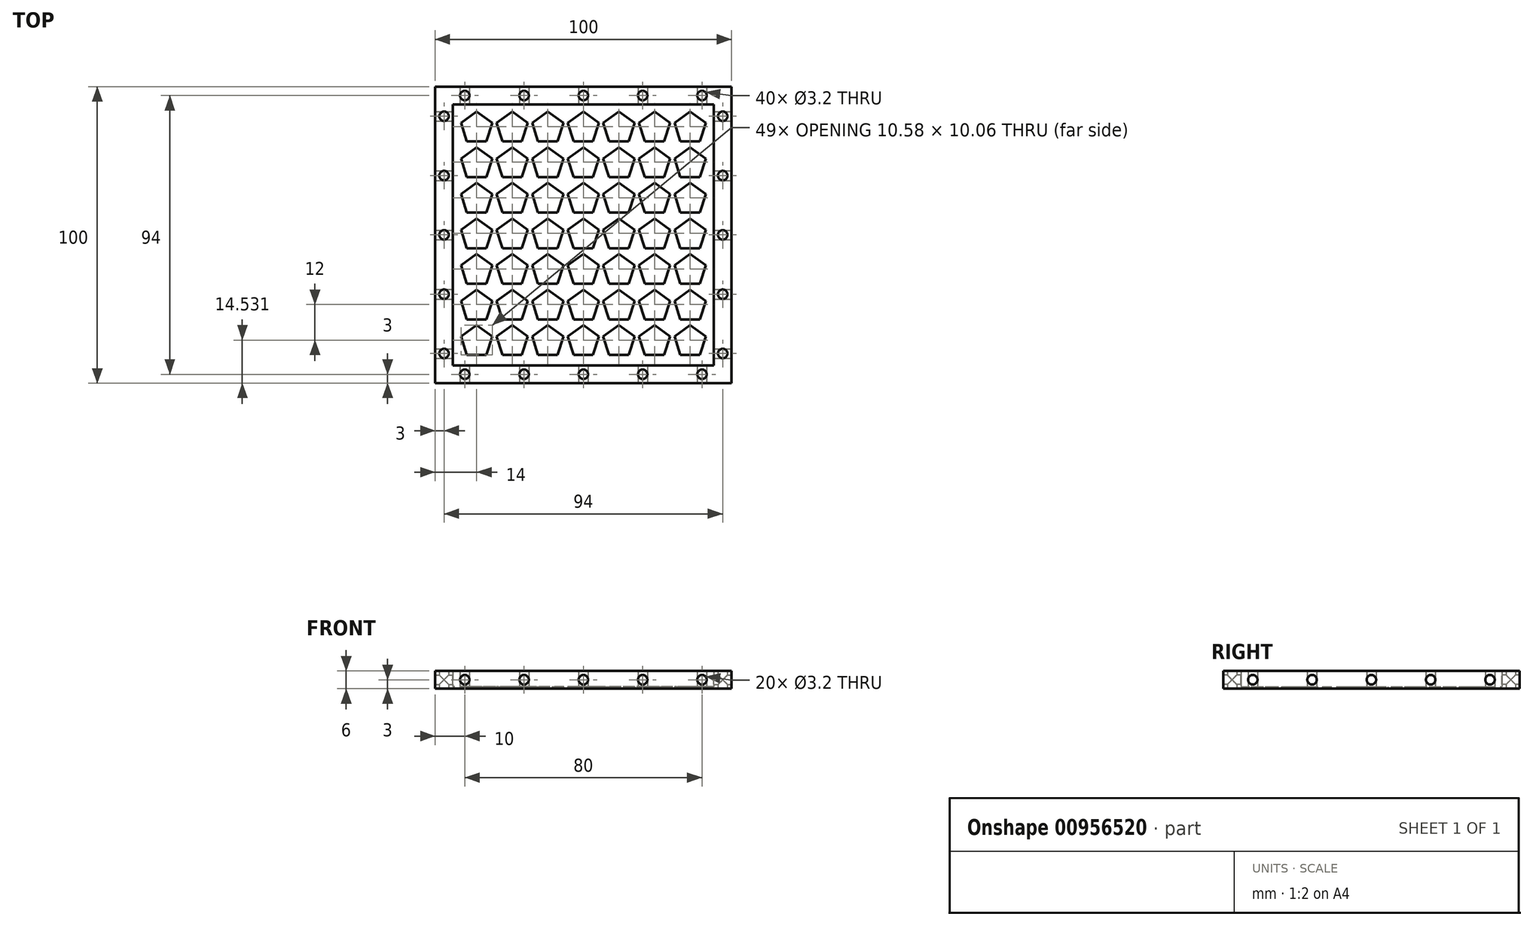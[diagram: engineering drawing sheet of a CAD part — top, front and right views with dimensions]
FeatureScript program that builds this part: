
annotation { "Feature Type Name" : "Feature", "Feature Type Description" : "" }
export const myFeature = defineFeature(function(context is Context, id is Id, definition is map)
    precondition{}
    {
        {
            var Q0;
            Q0=qCreatedBy(makeId("Top.planeOp"),FACE);
            var sketch = newSketch(context, id + "F0", { "sketchPlane" : qUnion([Q0])});
            skLineSegment(sketch, "E0.bottom", {"start": v(-50, 50) * mm, "end": v(50, 50) * mm});
            skLineSegment(sketch, "E0.top", {"start": v(-50, -50) * mm, "end": v(50, -50) * mm});
            skLineSegment(sketch, "E0.left", {"start": v(-50, 50) * mm, "end": v(-50, -50) * mm});
            skLineSegment(sketch, "E0.right", {"start": v(50, 50) * mm, "end": v(50, -50) * mm});
            skLineSegment(sketch, "E1", {"start": v(50, 50) * mm, "end": v(-50, -50) * mm, "construction": true});
            skLineSegment(sketch, "E2", {"start": v(-50, 50) * mm, "end": v(50, -50) * mm, "construction": true});
            skPoint(sketch, "E3", {"position": v(0, 0) * mm});
            skSolve(sketch);
        }
        {
            var Q0;
            Q0 = qSketchRegion(id + "F0", true);
            extrude(context, id + "F1", {"entities" : qUnion([Q0]), "depth" : .6 * mm, "offsetDistance" : 25 * mm});
        }
        {
            var Q0;
            Q0=qCreatedBy(makeId("Top.planeOp"),FACE);
            var sketch = newSketch(context, id + "F2", { "sketchPlane" : qUnion([Q0])});
            skLineSegment(sketch, "E4.bottom", {"start": v(-50, 50) * mm, "end": v(-44, 50) * mm});
            skLineSegment(sketch, "E4.top", {"start": v(-50, -50) * mm, "end": v(-44, -50) * mm});
            skLineSegment(sketch, "E4.left", {"start": v(-50, 50) * mm, "end": v(-50, -50) * mm});
            skLineSegment(sketch, "E4.right", {"start": v(-44, 50) * mm, "end": v(-44, -50) * mm});
            skLineSegment(sketch, "E5.MirrorCS", {"start": v(50, 50) * mm, "end": v(44, 50) * mm});
            skLineSegment(sketch, "E6.MirrorCS", {"start": v(50, -50) * mm, "end": v(44, -50) * mm});
            skLineSegment(sketch, "E7.MirrorCS", {"start": v(50, 50) * mm, "end": v(50, -50) * mm});
            skLineSegment(sketch, "E8.MirrorCS", {"start": v(44, 50) * mm, "end": v(44, -50) * mm});
            skLineSegment(sketch, "E9.bottom", {"start": v(-44, 50) * mm, "end": v(44, 50) * mm});
            skLineSegment(sketch, "E9.top", {"start": v(-44, 44) * mm, "end": v(44, 44) * mm});
            skLineSegment(sketch, "E9.left", {"start": v(-44, 50) * mm, "end": v(-44, 44) * mm});
            skLineSegment(sketch, "E9.right", {"start": v(44, 50) * mm, "end": v(44, 44) * mm});
            skLineSegment(sketch, "E10.MirrorCS", {"start": v(44, -50) * mm, "end": v(44, -44) * mm});
            skLineSegment(sketch, "E11.MirrorCS", {"start": v(-44, -50) * mm, "end": v(-44, -44) * mm});
            skLineSegment(sketch, "E12.MirrorCS", {"start": v(-44, -50) * mm, "end": v(44, -50) * mm});
            skLineSegment(sketch, "E13.MirrorCS", {"start": v(-44, -44) * mm, "end": v(44, -44) * mm});
            skSolve(sketch);
        }
        {
            var Q0;
            Q0 = qSketchRegion(id + "F2", true);
            extrude(context, id + "F3", {"entities" : qUnion([Q0]), "operationType" : NewBodyOperationType.ADD, "depth" : 6 * mm, "offsetDistance" : 25 * mm});
        }
        {
            var Q0;
            Q0=qCreatedBy(makeId("Top.planeOp"),FACE);
            var sketch = newSketch(context, id + "F4", { "sketchPlane" : qUnion([Q0])});
            skCircle(sketch, "E14.cCircle", {"center": v(-36, 36) * mm, "radius": 4.5 * mm, "construction": true});
            skLineSegment(sketch, "E14.0", {"start": v(-30.7, 37.72) * mm, "end": v(-32.73, 31.5) * mm});
            skLineSegment(sketch, "E14.1", {"start": v(-32.73, 31.5) * mm, "end": v(-39.27, 31.5) * mm});
            skLineSegment(sketch, "E14.2", {"start": v(-39.27, 31.5) * mm, "end": v(-41.3, 37.72) * mm});
            skLineSegment(sketch, "E14.3", {"start": v(-41.3, 37.72) * mm, "end": v(-36, 41.56) * mm});
            skLineSegment(sketch, "E14.4", {"start": v(-36, 41.56) * mm, "end": v(-30.7, 37.72) * mm});
            skPoint(sketch, "E14.0.midPoint", {"position": v(-31.72, 34.6) * mm});
            skLineSegment(sketch, "E15.0.1.0", {"start": v(-36, 29.56) * mm, "end": v(-30.7, 25.72) * mm});
            skLineSegment(sketch, "E15.0.1.1", {"start": v(-41.3, 25.72) * mm, "end": v(-36, 29.56) * mm});
            skPoint(sketch, "E15.0.1.2", {"position": v(-31.72, 22.6) * mm});
            skCircle(sketch, "E15.0.1.3", {"center": v(-36, 24) * mm, "radius": 4.5 * mm, "construction": true});
            skLineSegment(sketch, "E15.0.1.4", {"start": v(-30.7, 25.72) * mm, "end": v(-32.73, 19.5) * mm});
            skLineSegment(sketch, "E15.0.1.5", {"start": v(-32.73, 19.5) * mm, "end": v(-39.27, 19.5) * mm});
            skLineSegment(sketch, "E15.0.1.6", {"start": v(-39.27, 19.5) * mm, "end": v(-41.3, 25.72) * mm});
            skLineSegment(sketch, "E15.0.2.0", {"start": v(-36, 17.56) * mm, "end": v(-30.7, 13.72) * mm});
            skLineSegment(sketch, "E15.0.2.1", {"start": v(-41.3, 13.72) * mm, "end": v(-36, 17.56) * mm});
            skPoint(sketch, "E15.0.2.2", {"position": v(-31.72, 10.6) * mm});
            skCircle(sketch, "E15.0.2.3", {"center": v(-36, 12) * mm, "radius": 4.5 * mm, "construction": true});
            skLineSegment(sketch, "E15.0.2.4", {"start": v(-30.7, 13.72) * mm, "end": v(-32.73, 7.5) * mm});
            skLineSegment(sketch, "E15.0.2.5", {"start": v(-32.73, 7.5) * mm, "end": v(-39.27, 7.5) * mm});
            skLineSegment(sketch, "E15.0.2.6", {"start": v(-39.27, 7.5) * mm, "end": v(-41.3, 13.72) * mm});
            skLineSegment(sketch, "E15.0.3.0", {"start": v(-36, 5.56) * mm, "end": v(-30.7, 1.72) * mm});
            skLineSegment(sketch, "E15.0.3.1", {"start": v(-41.3, 1.72) * mm, "end": v(-36, 5.56) * mm});
            skPoint(sketch, "E15.0.3.2", {"position": v(-31.72, -1.4) * mm});
            skCircle(sketch, "E15.0.3.3", {"center": v(-36, 0) * mm, "radius": 4.5 * mm, "construction": true});
            skLineSegment(sketch, "E15.0.3.4", {"start": v(-30.7, 1.72) * mm, "end": v(-32.73, -4.5) * mm});
            skLineSegment(sketch, "E15.0.3.5", {"start": v(-32.73, -4.5) * mm, "end": v(-39.27, -4.5) * mm});
            skLineSegment(sketch, "E15.0.3.6", {"start": v(-39.27, -4.5) * mm, "end": v(-41.3, 1.72) * mm});
            skLineSegment(sketch, "E15.0.4.0", {"start": v(-36, -6.44) * mm, "end": v(-30.7, -10.28) * mm});
            skLineSegment(sketch, "E15.0.4.1", {"start": v(-41.3, -10.28) * mm, "end": v(-36, -6.44) * mm});
            skPoint(sketch, "E15.0.4.2", {"position": v(-31.72, -13.4) * mm});
            skCircle(sketch, "E15.0.4.3", {"center": v(-36, -12) * mm, "radius": 4.5 * mm, "construction": true});
            skLineSegment(sketch, "E15.0.4.4", {"start": v(-30.7, -10.28) * mm, "end": v(-32.73, -16.5) * mm});
            skLineSegment(sketch, "E15.0.4.5", {"start": v(-32.73, -16.5) * mm, "end": v(-39.27, -16.5) * mm});
            skLineSegment(sketch, "E15.0.4.6", {"start": v(-39.27, -16.5) * mm, "end": v(-41.3, -10.28) * mm});
            skLineSegment(sketch, "E15.0.5.0", {"start": v(-36, -18.44) * mm, "end": v(-30.7, -22.28) * mm});
            skLineSegment(sketch, "E15.0.5.1", {"start": v(-41.3, -22.28) * mm, "end": v(-36, -18.44) * mm});
            skPoint(sketch, "E15.0.5.2", {"position": v(-31.72, -25.4) * mm});
            skCircle(sketch, "E15.0.5.3", {"center": v(-36, -24) * mm, "radius": 4.5 * mm, "construction": true});
            skLineSegment(sketch, "E15.0.5.4", {"start": v(-30.7, -22.28) * mm, "end": v(-32.73, -28.5) * mm});
            skLineSegment(sketch, "E15.0.5.5", {"start": v(-32.73, -28.5) * mm, "end": v(-39.27, -28.5) * mm});
            skLineSegment(sketch, "E15.0.5.6", {"start": v(-39.27, -28.5) * mm, "end": v(-41.3, -22.28) * mm});
            skLineSegment(sketch, "E15.1.0.0", {"start": v(-24, 41.56) * mm, "end": v(-18.7, 37.72) * mm});
            skLineSegment(sketch, "E15.1.0.1", {"start": v(-29.3, 37.72) * mm, "end": v(-24, 41.56) * mm});
            skPoint(sketch, "E15.1.0.2", {"position": v(-19.72, 34.6) * mm});
            skCircle(sketch, "E15.1.0.3", {"center": v(-24, 36) * mm, "radius": 4.5 * mm, "construction": true});
            skLineSegment(sketch, "E15.1.0.4", {"start": v(-18.7, 37.72) * mm, "end": v(-20.73, 31.5) * mm});
            skLineSegment(sketch, "E15.1.0.5", {"start": v(-20.73, 31.5) * mm, "end": v(-27.27, 31.5) * mm});
            skLineSegment(sketch, "E15.1.0.6", {"start": v(-27.27, 31.5) * mm, "end": v(-29.3, 37.72) * mm});
            skLineSegment(sketch, "E15.1.1.0", {"start": v(-24, 29.56) * mm, "end": v(-18.7, 25.72) * mm});
            skLineSegment(sketch, "E15.1.1.1", {"start": v(-29.3, 25.72) * mm, "end": v(-24, 29.56) * mm});
            skPoint(sketch, "E15.1.1.2", {"position": v(-19.72, 22.6) * mm});
            skCircle(sketch, "E15.1.1.3", {"center": v(-24, 24) * mm, "radius": 4.5 * mm, "construction": true});
            skLineSegment(sketch, "E15.1.1.4", {"start": v(-18.7, 25.72) * mm, "end": v(-20.73, 19.5) * mm});
            skLineSegment(sketch, "E15.1.1.5", {"start": v(-20.73, 19.5) * mm, "end": v(-27.27, 19.5) * mm});
            skLineSegment(sketch, "E15.1.1.6", {"start": v(-27.27, 19.5) * mm, "end": v(-29.3, 25.72) * mm});
            skLineSegment(sketch, "E15.1.2.0", {"start": v(-24, 17.56) * mm, "end": v(-18.7, 13.72) * mm});
            skLineSegment(sketch, "E15.1.2.1", {"start": v(-29.3, 13.72) * mm, "end": v(-24, 17.56) * mm});
            skPoint(sketch, "E15.1.2.2", {"position": v(-19.72, 10.6) * mm});
            skCircle(sketch, "E15.1.2.3", {"center": v(-24, 12) * mm, "radius": 4.5 * mm, "construction": true});
            skLineSegment(sketch, "E15.1.2.4", {"start": v(-18.7, 13.72) * mm, "end": v(-20.73, 7.5) * mm});
            skLineSegment(sketch, "E15.1.2.5", {"start": v(-20.73, 7.5) * mm, "end": v(-27.27, 7.5) * mm});
            skLineSegment(sketch, "E15.1.2.6", {"start": v(-27.27, 7.5) * mm, "end": v(-29.3, 13.72) * mm});
            skLineSegment(sketch, "E15.1.3.0", {"start": v(-24, 5.56) * mm, "end": v(-18.7, 1.72) * mm});
            skLineSegment(sketch, "E15.1.3.1", {"start": v(-29.3, 1.72) * mm, "end": v(-24, 5.56) * mm});
            skPoint(sketch, "E15.1.3.2", {"position": v(-19.72, -1.4) * mm});
            skCircle(sketch, "E15.1.3.3", {"center": v(-24, 0) * mm, "radius": 4.5 * mm, "construction": true});
            skLineSegment(sketch, "E15.1.3.4", {"start": v(-18.7, 1.72) * mm, "end": v(-20.73, -4.5) * mm});
            skLineSegment(sketch, "E15.1.3.5", {"start": v(-20.73, -4.5) * mm, "end": v(-27.27, -4.5) * mm});
            skLineSegment(sketch, "E15.1.3.6", {"start": v(-27.27, -4.5) * mm, "end": v(-29.3, 1.72) * mm});
            skLineSegment(sketch, "E15.1.4.0", {"start": v(-24, -6.44) * mm, "end": v(-18.7, -10.28) * mm});
            skLineSegment(sketch, "E15.1.4.1", {"start": v(-29.3, -10.28) * mm, "end": v(-24, -6.44) * mm});
            skPoint(sketch, "E15.1.4.2", {"position": v(-19.72, -13.4) * mm});
            skCircle(sketch, "E15.1.4.3", {"center": v(-24, -12) * mm, "radius": 4.5 * mm, "construction": true});
            skLineSegment(sketch, "E15.1.4.4", {"start": v(-18.7, -10.28) * mm, "end": v(-20.73, -16.5) * mm});
            skLineSegment(sketch, "E15.1.4.5", {"start": v(-20.73, -16.5) * mm, "end": v(-27.27, -16.5) * mm});
            skLineSegment(sketch, "E15.1.4.6", {"start": v(-27.27, -16.5) * mm, "end": v(-29.3, -10.28) * mm});
            skLineSegment(sketch, "E15.1.5.0", {"start": v(-24, -18.44) * mm, "end": v(-18.7, -22.28) * mm});
            skLineSegment(sketch, "E15.1.5.1", {"start": v(-29.3, -22.28) * mm, "end": v(-24, -18.44) * mm});
            skPoint(sketch, "E15.1.5.2", {"position": v(-19.72, -25.4) * mm});
            skCircle(sketch, "E15.1.5.3", {"center": v(-24, -24) * mm, "radius": 4.5 * mm, "construction": true});
            skLineSegment(sketch, "E15.1.5.4", {"start": v(-18.7, -22.28) * mm, "end": v(-20.73, -28.5) * mm});
            skLineSegment(sketch, "E15.1.5.5", {"start": v(-20.73, -28.5) * mm, "end": v(-27.27, -28.5) * mm});
            skLineSegment(sketch, "E15.1.5.6", {"start": v(-27.27, -28.5) * mm, "end": v(-29.3, -22.28) * mm});
            skLineSegment(sketch, "E15.2.0.0", {"start": v(-12, 41.56) * mm, "end": v(-6.7, 37.72) * mm});
            skLineSegment(sketch, "E15.2.0.1", {"start": v(-17.3, 37.72) * mm, "end": v(-12, 41.56) * mm});
            skPoint(sketch, "E15.2.0.2", {"position": v(-7.72, 34.6) * mm});
            skCircle(sketch, "E15.2.0.3", {"center": v(-12, 36) * mm, "radius": 4.5 * mm, "construction": true});
            skLineSegment(sketch, "E15.2.0.4", {"start": v(-6.7, 37.72) * mm, "end": v(-8.73, 31.5) * mm});
            skLineSegment(sketch, "E15.2.0.5", {"start": v(-8.73, 31.5) * mm, "end": v(-15.27, 31.5) * mm});
            skLineSegment(sketch, "E15.2.0.6", {"start": v(-15.27, 31.5) * mm, "end": v(-17.3, 37.72) * mm});
            skLineSegment(sketch, "E15.2.1.0", {"start": v(-12, 29.56) * mm, "end": v(-6.7, 25.72) * mm});
            skLineSegment(sketch, "E15.2.1.1", {"start": v(-17.3, 25.72) * mm, "end": v(-12, 29.56) * mm});
            skPoint(sketch, "E15.2.1.2", {"position": v(-7.72, 22.6) * mm});
            skCircle(sketch, "E15.2.1.3", {"center": v(-12, 24) * mm, "radius": 4.5 * mm, "construction": true});
            skLineSegment(sketch, "E15.2.1.4", {"start": v(-6.7, 25.72) * mm, "end": v(-8.73, 19.5) * mm});
            skLineSegment(sketch, "E15.2.1.5", {"start": v(-8.73, 19.5) * mm, "end": v(-15.27, 19.5) * mm});
            skLineSegment(sketch, "E15.2.1.6", {"start": v(-15.27, 19.5) * mm, "end": v(-17.3, 25.72) * mm});
            skLineSegment(sketch, "E15.2.2.0", {"start": v(-12, 17.56) * mm, "end": v(-6.7, 13.72) * mm});
            skLineSegment(sketch, "E15.2.2.1", {"start": v(-17.3, 13.72) * mm, "end": v(-12, 17.56) * mm});
            skPoint(sketch, "E15.2.2.2", {"position": v(-7.72, 10.6) * mm});
            skCircle(sketch, "E15.2.2.3", {"center": v(-12, 12) * mm, "radius": 4.5 * mm, "construction": true});
            skLineSegment(sketch, "E15.2.2.4", {"start": v(-6.7, 13.72) * mm, "end": v(-8.73, 7.5) * mm});
            skLineSegment(sketch, "E15.2.2.5", {"start": v(-8.73, 7.5) * mm, "end": v(-15.27, 7.5) * mm});
            skLineSegment(sketch, "E15.2.2.6", {"start": v(-15.27, 7.5) * mm, "end": v(-17.3, 13.72) * mm});
            skLineSegment(sketch, "E15.2.3.0", {"start": v(-12, 5.56) * mm, "end": v(-6.7, 1.72) * mm});
            skLineSegment(sketch, "E15.2.3.1", {"start": v(-17.3, 1.72) * mm, "end": v(-12, 5.56) * mm});
            skPoint(sketch, "E15.2.3.2", {"position": v(-7.72, -1.4) * mm});
            skCircle(sketch, "E15.2.3.3", {"center": v(-12, 0) * mm, "radius": 4.5 * mm, "construction": true});
            skLineSegment(sketch, "E15.2.3.4", {"start": v(-6.7, 1.72) * mm, "end": v(-8.73, -4.5) * mm});
            skLineSegment(sketch, "E15.2.3.5", {"start": v(-8.73, -4.5) * mm, "end": v(-15.27, -4.5) * mm});
            skLineSegment(sketch, "E15.2.3.6", {"start": v(-15.27, -4.5) * mm, "end": v(-17.3, 1.72) * mm});
            skLineSegment(sketch, "E15.2.4.0", {"start": v(-12, -6.44) * mm, "end": v(-6.7, -10.28) * mm});
            skLineSegment(sketch, "E15.2.4.1", {"start": v(-17.3, -10.28) * mm, "end": v(-12, -6.44) * mm});
            skPoint(sketch, "E15.2.4.2", {"position": v(-7.72, -13.4) * mm});
            skCircle(sketch, "E15.2.4.3", {"center": v(-12, -12) * mm, "radius": 4.5 * mm, "construction": true});
            skLineSegment(sketch, "E15.2.4.4", {"start": v(-6.7, -10.28) * mm, "end": v(-8.73, -16.5) * mm});
            skLineSegment(sketch, "E15.2.4.5", {"start": v(-8.73, -16.5) * mm, "end": v(-15.27, -16.5) * mm});
            skLineSegment(sketch, "E15.2.4.6", {"start": v(-15.27, -16.5) * mm, "end": v(-17.3, -10.28) * mm});
            skLineSegment(sketch, "E15.2.5.0", {"start": v(-12, -18.44) * mm, "end": v(-6.7, -22.28) * mm});
            skLineSegment(sketch, "E15.2.5.1", {"start": v(-17.3, -22.28) * mm, "end": v(-12, -18.44) * mm});
            skPoint(sketch, "E15.2.5.2", {"position": v(-7.72, -25.4) * mm});
            skCircle(sketch, "E15.2.5.3", {"center": v(-12, -24) * mm, "radius": 4.5 * mm, "construction": true});
            skLineSegment(sketch, "E15.2.5.4", {"start": v(-6.7, -22.28) * mm, "end": v(-8.73, -28.5) * mm});
            skLineSegment(sketch, "E15.2.5.5", {"start": v(-8.73, -28.5) * mm, "end": v(-15.27, -28.5) * mm});
            skLineSegment(sketch, "E15.2.5.6", {"start": v(-15.27, -28.5) * mm, "end": v(-17.3, -22.28) * mm});
            skLineSegment(sketch, "E15.3.0.0", {"start": v(0, 41.56) * mm, "end": v(5.3, 37.72) * mm});
            skLineSegment(sketch, "E15.3.0.1", {"start": v(-5.3, 37.72) * mm, "end": v(0, 41.56) * mm});
            skPoint(sketch, "E15.3.0.2", {"position": v(4.28, 34.6) * mm});
            skCircle(sketch, "E15.3.0.3", {"center": v(0, 36) * mm, "radius": 4.5 * mm, "construction": true});
            skLineSegment(sketch, "E15.3.0.4", {"start": v(5.3, 37.72) * mm, "end": v(3.27, 31.5) * mm});
            skLineSegment(sketch, "E15.3.0.5", {"start": v(3.27, 31.5) * mm, "end": v(-3.27, 31.5) * mm});
            skLineSegment(sketch, "E15.3.0.6", {"start": v(-3.27, 31.5) * mm, "end": v(-5.3, 37.72) * mm});
            skLineSegment(sketch, "E15.3.1.0", {"start": v(0, 29.56) * mm, "end": v(5.3, 25.72) * mm});
            skLineSegment(sketch, "E15.3.1.1", {"start": v(-5.3, 25.72) * mm, "end": v(0, 29.56) * mm});
            skPoint(sketch, "E15.3.1.2", {"position": v(4.28, 22.6) * mm});
            skCircle(sketch, "E15.3.1.3", {"center": v(0, 24) * mm, "radius": 4.5 * mm, "construction": true});
            skLineSegment(sketch, "E15.3.1.4", {"start": v(5.3, 25.72) * mm, "end": v(3.27, 19.5) * mm});
            skLineSegment(sketch, "E15.3.1.5", {"start": v(3.27, 19.5) * mm, "end": v(-3.27, 19.5) * mm});
            skLineSegment(sketch, "E15.3.1.6", {"start": v(-3.27, 19.5) * mm, "end": v(-5.3, 25.72) * mm});
            skLineSegment(sketch, "E15.3.2.0", {"start": v(0, 17.56) * mm, "end": v(5.3, 13.72) * mm});
            skLineSegment(sketch, "E15.3.2.1", {"start": v(-5.3, 13.72) * mm, "end": v(0, 17.56) * mm});
            skPoint(sketch, "E15.3.2.2", {"position": v(4.28, 10.6) * mm});
            skCircle(sketch, "E15.3.2.3", {"center": v(0, 12) * mm, "radius": 4.5 * mm, "construction": true});
            skLineSegment(sketch, "E15.3.2.4", {"start": v(5.3, 13.72) * mm, "end": v(3.27, 7.5) * mm});
            skLineSegment(sketch, "E15.3.2.5", {"start": v(3.27, 7.5) * mm, "end": v(-3.27, 7.5) * mm});
            skLineSegment(sketch, "E15.3.2.6", {"start": v(-3.27, 7.5) * mm, "end": v(-5.3, 13.72) * mm});
            skLineSegment(sketch, "E15.3.3.0", {"start": v(0, 5.56) * mm, "end": v(5.3, 1.72) * mm});
            skLineSegment(sketch, "E15.3.3.1", {"start": v(-5.3, 1.72) * mm, "end": v(0, 5.56) * mm});
            skPoint(sketch, "E15.3.3.2", {"position": v(4.28, -1.4) * mm});
            skCircle(sketch, "E15.3.3.3", {"center": v(0, 0) * mm, "radius": 4.5 * mm, "construction": true});
            skLineSegment(sketch, "E15.3.3.4", {"start": v(5.3, 1.72) * mm, "end": v(3.27, -4.5) * mm});
            skLineSegment(sketch, "E15.3.3.5", {"start": v(3.27, -4.5) * mm, "end": v(-3.27, -4.5) * mm});
            skLineSegment(sketch, "E15.3.3.6", {"start": v(-3.27, -4.5) * mm, "end": v(-5.3, 1.72) * mm});
            skLineSegment(sketch, "E15.3.4.0", {"start": v(0, -6.44) * mm, "end": v(5.3, -10.28) * mm});
            skLineSegment(sketch, "E15.3.4.1", {"start": v(-5.3, -10.28) * mm, "end": v(0, -6.44) * mm});
            skPoint(sketch, "E15.3.4.2", {"position": v(4.28, -13.4) * mm});
            skCircle(sketch, "E15.3.4.3", {"center": v(0, -12) * mm, "radius": 4.5 * mm, "construction": true});
            skLineSegment(sketch, "E15.3.4.4", {"start": v(5.3, -10.28) * mm, "end": v(3.27, -16.5) * mm});
            skLineSegment(sketch, "E15.3.4.5", {"start": v(3.27, -16.5) * mm, "end": v(-3.27, -16.5) * mm});
            skLineSegment(sketch, "E15.3.4.6", {"start": v(-3.27, -16.5) * mm, "end": v(-5.3, -10.28) * mm});
            skLineSegment(sketch, "E15.3.5.0", {"start": v(0, -18.44) * mm, "end": v(5.3, -22.28) * mm});
            skLineSegment(sketch, "E15.3.5.1", {"start": v(-5.3, -22.28) * mm, "end": v(0, -18.44) * mm});
            skPoint(sketch, "E15.3.5.2", {"position": v(4.28, -25.4) * mm});
            skCircle(sketch, "E15.3.5.3", {"center": v(0, -24) * mm, "radius": 4.5 * mm, "construction": true});
            skLineSegment(sketch, "E15.3.5.4", {"start": v(5.3, -22.28) * mm, "end": v(3.27, -28.5) * mm});
            skLineSegment(sketch, "E15.3.5.5", {"start": v(3.27, -28.5) * mm, "end": v(-3.27, -28.5) * mm});
            skLineSegment(sketch, "E15.3.5.6", {"start": v(-3.27, -28.5) * mm, "end": v(-5.3, -22.28) * mm});
            skLineSegment(sketch, "E15.4.0.0", {"start": v(12, 41.56) * mm, "end": v(17.3, 37.72) * mm});
            skLineSegment(sketch, "E15.4.0.1", {"start": v(6.7, 37.72) * mm, "end": v(12, 41.56) * mm});
            skPoint(sketch, "E15.4.0.2", {"position": v(16.28, 34.6) * mm});
            skCircle(sketch, "E15.4.0.3", {"center": v(12, 36) * mm, "radius": 4.5 * mm, "construction": true});
            skLineSegment(sketch, "E15.4.0.4", {"start": v(17.3, 37.72) * mm, "end": v(15.27, 31.5) * mm});
            skLineSegment(sketch, "E15.4.0.5", {"start": v(15.27, 31.5) * mm, "end": v(8.73, 31.5) * mm});
            skLineSegment(sketch, "E15.4.0.6", {"start": v(8.73, 31.5) * mm, "end": v(6.7, 37.72) * mm});
            skLineSegment(sketch, "E15.4.1.0", {"start": v(12, 29.56) * mm, "end": v(17.3, 25.72) * mm});
            skLineSegment(sketch, "E15.4.1.1", {"start": v(6.7, 25.72) * mm, "end": v(12, 29.56) * mm});
            skPoint(sketch, "E15.4.1.2", {"position": v(16.28, 22.6) * mm});
            skCircle(sketch, "E15.4.1.3", {"center": v(12, 24) * mm, "radius": 4.5 * mm, "construction": true});
            skLineSegment(sketch, "E15.4.1.4", {"start": v(17.3, 25.72) * mm, "end": v(15.27, 19.5) * mm});
            skLineSegment(sketch, "E15.4.1.5", {"start": v(15.27, 19.5) * mm, "end": v(8.73, 19.5) * mm});
            skLineSegment(sketch, "E15.4.1.6", {"start": v(8.73, 19.5) * mm, "end": v(6.7, 25.72) * mm});
            skLineSegment(sketch, "E15.4.2.0", {"start": v(12, 17.56) * mm, "end": v(17.3, 13.72) * mm});
            skLineSegment(sketch, "E15.4.2.1", {"start": v(6.7, 13.72) * mm, "end": v(12, 17.56) * mm});
            skPoint(sketch, "E15.4.2.2", {"position": v(16.28, 10.6) * mm});
            skCircle(sketch, "E15.4.2.3", {"center": v(12, 12) * mm, "radius": 4.5 * mm, "construction": true});
            skLineSegment(sketch, "E15.4.2.4", {"start": v(17.3, 13.72) * mm, "end": v(15.27, 7.5) * mm});
            skLineSegment(sketch, "E15.4.2.5", {"start": v(15.27, 7.5) * mm, "end": v(8.73, 7.5) * mm});
            skLineSegment(sketch, "E15.4.2.6", {"start": v(8.73, 7.5) * mm, "end": v(6.7, 13.72) * mm});
            skLineSegment(sketch, "E15.4.3.0", {"start": v(12, 5.56) * mm, "end": v(17.3, 1.72) * mm});
            skLineSegment(sketch, "E15.4.3.1", {"start": v(6.7, 1.72) * mm, "end": v(12, 5.56) * mm});
            skPoint(sketch, "E15.4.3.2", {"position": v(16.28, -1.4) * mm});
            skCircle(sketch, "E15.4.3.3", {"center": v(12, 0) * mm, "radius": 4.5 * mm, "construction": true});
            skLineSegment(sketch, "E15.4.3.4", {"start": v(17.3, 1.72) * mm, "end": v(15.27, -4.5) * mm});
            skLineSegment(sketch, "E15.4.3.5", {"start": v(15.27, -4.5) * mm, "end": v(8.73, -4.5) * mm});
            skLineSegment(sketch, "E15.4.3.6", {"start": v(8.73, -4.5) * mm, "end": v(6.7, 1.72) * mm});
            skLineSegment(sketch, "E15.4.4.0", {"start": v(12, -6.44) * mm, "end": v(17.3, -10.28) * mm});
            skLineSegment(sketch, "E15.4.4.1", {"start": v(6.7, -10.28) * mm, "end": v(12, -6.44) * mm});
            skPoint(sketch, "E15.4.4.2", {"position": v(16.28, -13.4) * mm});
            skCircle(sketch, "E15.4.4.3", {"center": v(12, -12) * mm, "radius": 4.5 * mm, "construction": true});
            skLineSegment(sketch, "E15.4.4.4", {"start": v(17.3, -10.28) * mm, "end": v(15.27, -16.5) * mm});
            skLineSegment(sketch, "E15.4.4.5", {"start": v(15.27, -16.5) * mm, "end": v(8.73, -16.5) * mm});
            skLineSegment(sketch, "E15.4.4.6", {"start": v(8.73, -16.5) * mm, "end": v(6.7, -10.28) * mm});
            skLineSegment(sketch, "E15.4.5.0", {"start": v(12, -18.44) * mm, "end": v(17.3, -22.28) * mm});
            skLineSegment(sketch, "E15.4.5.1", {"start": v(6.7, -22.28) * mm, "end": v(12, -18.44) * mm});
            skPoint(sketch, "E15.4.5.2", {"position": v(16.28, -25.4) * mm});
            skCircle(sketch, "E15.4.5.3", {"center": v(12, -24) * mm, "radius": 4.5 * mm, "construction": true});
            skLineSegment(sketch, "E15.4.5.4", {"start": v(17.3, -22.28) * mm, "end": v(15.27, -28.5) * mm});
            skLineSegment(sketch, "E15.4.5.5", {"start": v(15.27, -28.5) * mm, "end": v(8.73, -28.5) * mm});
            skLineSegment(sketch, "E15.4.5.6", {"start": v(8.73, -28.5) * mm, "end": v(6.7, -22.28) * mm});
            skLineSegment(sketch, "E15.5.0.0", {"start": v(24, 41.56) * mm, "end": v(29.3, 37.72) * mm});
            skLineSegment(sketch, "E15.5.0.1", {"start": v(18.7, 37.72) * mm, "end": v(24, 41.56) * mm});
            skPoint(sketch, "E15.5.0.2", {"position": v(28.28, 34.6) * mm});
            skCircle(sketch, "E15.5.0.3", {"center": v(24, 36) * mm, "radius": 4.5 * mm, "construction": true});
            skLineSegment(sketch, "E15.5.0.4", {"start": v(29.3, 37.72) * mm, "end": v(27.27, 31.5) * mm});
            skLineSegment(sketch, "E15.5.0.5", {"start": v(27.27, 31.5) * mm, "end": v(20.73, 31.5) * mm});
            skLineSegment(sketch, "E15.5.0.6", {"start": v(20.73, 31.5) * mm, "end": v(18.7, 37.72) * mm});
            skLineSegment(sketch, "E15.5.1.0", {"start": v(24, 29.56) * mm, "end": v(29.3, 25.72) * mm});
            skLineSegment(sketch, "E15.5.1.1", {"start": v(18.7, 25.72) * mm, "end": v(24, 29.56) * mm});
            skPoint(sketch, "E15.5.1.2", {"position": v(28.28, 22.6) * mm});
            skCircle(sketch, "E15.5.1.3", {"center": v(24, 24) * mm, "radius": 4.5 * mm, "construction": true});
            skLineSegment(sketch, "E15.5.1.4", {"start": v(29.3, 25.72) * mm, "end": v(27.27, 19.5) * mm});
            skLineSegment(sketch, "E15.5.1.5", {"start": v(27.27, 19.5) * mm, "end": v(20.73, 19.5) * mm});
            skLineSegment(sketch, "E15.5.1.6", {"start": v(20.73, 19.5) * mm, "end": v(18.7, 25.72) * mm});
            skLineSegment(sketch, "E15.5.2.0", {"start": v(24, 17.56) * mm, "end": v(29.3, 13.72) * mm});
            skLineSegment(sketch, "E15.5.2.1", {"start": v(18.7, 13.72) * mm, "end": v(24, 17.56) * mm});
            skPoint(sketch, "E15.5.2.2", {"position": v(28.28, 10.6) * mm});
            skCircle(sketch, "E15.5.2.3", {"center": v(24, 12) * mm, "radius": 4.5 * mm, "construction": true});
            skLineSegment(sketch, "E15.5.2.4", {"start": v(29.3, 13.72) * mm, "end": v(27.27, 7.5) * mm});
            skLineSegment(sketch, "E15.5.2.5", {"start": v(27.27, 7.5) * mm, "end": v(20.73, 7.5) * mm});
            skLineSegment(sketch, "E15.5.2.6", {"start": v(20.73, 7.5) * mm, "end": v(18.7, 13.72) * mm});
            skLineSegment(sketch, "E15.5.3.0", {"start": v(24, 5.56) * mm, "end": v(29.3, 1.72) * mm});
            skLineSegment(sketch, "E15.5.3.1", {"start": v(18.7, 1.72) * mm, "end": v(24, 5.56) * mm});
            skPoint(sketch, "E15.5.3.2", {"position": v(28.28, -1.4) * mm});
            skCircle(sketch, "E15.5.3.3", {"center": v(24, 0) * mm, "radius": 4.5 * mm, "construction": true});
            skLineSegment(sketch, "E15.5.3.4", {"start": v(29.3, 1.72) * mm, "end": v(27.27, -4.5) * mm});
            skLineSegment(sketch, "E15.5.3.5", {"start": v(27.27, -4.5) * mm, "end": v(20.73, -4.5) * mm});
            skLineSegment(sketch, "E15.5.3.6", {"start": v(20.73, -4.5) * mm, "end": v(18.7, 1.72) * mm});
            skLineSegment(sketch, "E15.5.4.0", {"start": v(24, -6.44) * mm, "end": v(29.3, -10.28) * mm});
            skLineSegment(sketch, "E15.5.4.1", {"start": v(18.7, -10.28) * mm, "end": v(24, -6.44) * mm});
            skPoint(sketch, "E15.5.4.2", {"position": v(28.28, -13.4) * mm});
            skCircle(sketch, "E15.5.4.3", {"center": v(24, -12) * mm, "radius": 4.5 * mm, "construction": true});
            skLineSegment(sketch, "E15.5.4.4", {"start": v(29.3, -10.28) * mm, "end": v(27.27, -16.5) * mm});
            skLineSegment(sketch, "E15.5.4.5", {"start": v(27.27, -16.5) * mm, "end": v(20.73, -16.5) * mm});
            skLineSegment(sketch, "E15.5.4.6", {"start": v(20.73, -16.5) * mm, "end": v(18.7, -10.28) * mm});
            skLineSegment(sketch, "E15.5.5.0", {"start": v(24, -18.44) * mm, "end": v(29.3, -22.28) * mm});
            skLineSegment(sketch, "E15.5.5.1", {"start": v(18.7, -22.28) * mm, "end": v(24, -18.44) * mm});
            skPoint(sketch, "E15.5.5.2", {"position": v(28.28, -25.4) * mm});
            skCircle(sketch, "E15.5.5.3", {"center": v(24, -24) * mm, "radius": 4.5 * mm, "construction": true});
            skLineSegment(sketch, "E15.5.5.4", {"start": v(29.3, -22.28) * mm, "end": v(27.27, -28.5) * mm});
            skLineSegment(sketch, "E15.5.5.5", {"start": v(27.27, -28.5) * mm, "end": v(20.73, -28.5) * mm});
            skLineSegment(sketch, "E15.5.5.6", {"start": v(20.73, -28.5) * mm, "end": v(18.7, -22.28) * mm});
            skLineSegment(sketch, "E15.direction1", {"start": v(-39.27, 31.5) * mm, "end": v(-27.27, 31.5) * mm, "construction": true});
            skLineSegment(sketch, "E15.direction2", {"start": v(-39.27, 31.5) * mm, "end": v(-39.27, 19.5) * mm, "construction": true});
            skLineSegment(sketch, "E16.0.6.0", {"start": v(36, 41.56) * mm, "end": v(41.3, 37.72) * mm});
            skLineSegment(sketch, "E16.3.6.0", {"start": v(30.7, 37.72) * mm, "end": v(36, 41.56) * mm});
            skPoint(sketch, "E16.6.6.0", {"position": v(40.28, 34.6) * mm});
            skCircle(sketch, "E16.7.6.0", {"center": v(36, 36) * mm, "radius": 4.5 * mm, "construction": true});
            skLineSegment(sketch, "E16.9.6.0", {"start": v(41.3, 37.72) * mm, "end": v(39.27, 31.5) * mm});
            skLineSegment(sketch, "E16.12.6.0", {"start": v(39.27, 31.5) * mm, "end": v(32.73, 31.5) * mm});
            skLineSegment(sketch, "E16.15.6.0", {"start": v(32.73, 31.5) * mm, "end": v(30.7, 37.72) * mm});
            skLineSegment(sketch, "E16.0.6.1", {"start": v(36, 29.56) * mm, "end": v(41.3, 25.72) * mm});
            skLineSegment(sketch, "E16.3.6.1", {"start": v(30.7, 25.72) * mm, "end": v(36, 29.56) * mm});
            skPoint(sketch, "E16.6.6.1", {"position": v(40.28, 22.6) * mm});
            skCircle(sketch, "E16.7.6.1", {"center": v(36, 24) * mm, "radius": 4.5 * mm, "construction": true});
            skLineSegment(sketch, "E16.9.6.1", {"start": v(41.3, 25.72) * mm, "end": v(39.27, 19.5) * mm});
            skLineSegment(sketch, "E16.12.6.1", {"start": v(39.27, 19.5) * mm, "end": v(32.73, 19.5) * mm});
            skLineSegment(sketch, "E16.15.6.1", {"start": v(32.73, 19.5) * mm, "end": v(30.7, 25.72) * mm});
            skLineSegment(sketch, "E16.0.6.2", {"start": v(36, 17.56) * mm, "end": v(41.3, 13.72) * mm});
            skLineSegment(sketch, "E16.3.6.2", {"start": v(30.7, 13.72) * mm, "end": v(36, 17.56) * mm});
            skPoint(sketch, "E16.6.6.2", {"position": v(40.28, 10.6) * mm});
            skCircle(sketch, "E16.7.6.2", {"center": v(36, 12) * mm, "radius": 4.5 * mm, "construction": true});
            skLineSegment(sketch, "E16.9.6.2", {"start": v(41.3, 13.72) * mm, "end": v(39.27, 7.5) * mm});
            skLineSegment(sketch, "E16.12.6.2", {"start": v(39.27, 7.5) * mm, "end": v(32.73, 7.5) * mm});
            skLineSegment(sketch, "E16.15.6.2", {"start": v(32.73, 7.5) * mm, "end": v(30.7, 13.72) * mm});
            skLineSegment(sketch, "E16.0.6.3", {"start": v(36, 5.56) * mm, "end": v(41.3, 1.72) * mm});
            skLineSegment(sketch, "E16.3.6.3", {"start": v(30.7, 1.72) * mm, "end": v(36, 5.56) * mm});
            skPoint(sketch, "E16.6.6.3", {"position": v(40.28, -1.4) * mm});
            skCircle(sketch, "E16.7.6.3", {"center": v(36, 0) * mm, "radius": 4.5 * mm, "construction": true});
            skLineSegment(sketch, "E16.9.6.3", {"start": v(41.3, 1.72) * mm, "end": v(39.27, -4.5) * mm});
            skLineSegment(sketch, "E16.12.6.3", {"start": v(39.27, -4.5) * mm, "end": v(32.73, -4.5) * mm});
            skLineSegment(sketch, "E16.15.6.3", {"start": v(32.73, -4.5) * mm, "end": v(30.7, 1.72) * mm});
            skLineSegment(sketch, "E16.0.6.4", {"start": v(36, -6.44) * mm, "end": v(41.3, -10.28) * mm});
            skLineSegment(sketch, "E16.3.6.4", {"start": v(30.7, -10.28) * mm, "end": v(36, -6.44) * mm});
            skPoint(sketch, "E16.6.6.4", {"position": v(40.28, -13.4) * mm});
            skCircle(sketch, "E16.7.6.4", {"center": v(36, -12) * mm, "radius": 4.5 * mm, "construction": true});
            skLineSegment(sketch, "E16.9.6.4", {"start": v(41.3, -10.28) * mm, "end": v(39.27, -16.5) * mm});
            skLineSegment(sketch, "E16.12.6.4", {"start": v(39.27, -16.5) * mm, "end": v(32.73, -16.5) * mm});
            skLineSegment(sketch, "E16.15.6.4", {"start": v(32.73, -16.5) * mm, "end": v(30.7, -10.28) * mm});
            skLineSegment(sketch, "E16.0.6.5", {"start": v(36, -18.44) * mm, "end": v(41.3, -22.28) * mm});
            skLineSegment(sketch, "E16.3.6.5", {"start": v(30.7, -22.28) * mm, "end": v(36, -18.44) * mm});
            skPoint(sketch, "E16.6.6.5", {"position": v(40.28, -25.4) * mm});
            skCircle(sketch, "E16.7.6.5", {"center": v(36, -24) * mm, "radius": 4.5 * mm, "construction": true});
            skLineSegment(sketch, "E16.9.6.5", {"start": v(41.3, -22.28) * mm, "end": v(39.27, -28.5) * mm});
            skLineSegment(sketch, "E16.12.6.5", {"start": v(39.27, -28.5) * mm, "end": v(32.73, -28.5) * mm});
            skLineSegment(sketch, "E16.15.6.5", {"start": v(32.73, -28.5) * mm, "end": v(30.7, -22.28) * mm});
            skLineSegment(sketch, "E17.0.0.6", {"start": v(-36, -30.44) * mm, "end": v(-30.7, -34.28) * mm});
            skLineSegment(sketch, "E17.3.0.6", {"start": v(-41.3, -34.28) * mm, "end": v(-36, -30.44) * mm});
            skPoint(sketch, "E17.6.0.6", {"position": v(-31.72, -37.4) * mm});
            skCircle(sketch, "E17.7.0.6", {"center": v(-36, -36) * mm, "radius": 4.5 * mm, "construction": true});
            skLineSegment(sketch, "E17.9.0.6", {"start": v(-30.7, -34.28) * mm, "end": v(-32.73, -40.5) * mm});
            skLineSegment(sketch, "E17.12.0.6", {"start": v(-32.73, -40.5) * mm, "end": v(-39.27, -40.5) * mm});
            skLineSegment(sketch, "E17.15.0.6", {"start": v(-39.27, -40.5) * mm, "end": v(-41.3, -34.28) * mm});
            skLineSegment(sketch, "E17.0.1.6", {"start": v(-24, -30.44) * mm, "end": v(-18.7, -34.28) * mm});
            skLineSegment(sketch, "E17.3.1.6", {"start": v(-29.3, -34.28) * mm, "end": v(-24, -30.44) * mm});
            skPoint(sketch, "E17.6.1.6", {"position": v(-19.72, -37.4) * mm});
            skCircle(sketch, "E17.7.1.6", {"center": v(-24, -36) * mm, "radius": 4.5 * mm, "construction": true});
            skLineSegment(sketch, "E17.9.1.6", {"start": v(-18.7, -34.28) * mm, "end": v(-20.73, -40.5) * mm});
            skLineSegment(sketch, "E17.12.1.6", {"start": v(-20.73, -40.5) * mm, "end": v(-27.27, -40.5) * mm});
            skLineSegment(sketch, "E17.15.1.6", {"start": v(-27.27, -40.5) * mm, "end": v(-29.3, -34.28) * mm});
            skLineSegment(sketch, "E17.0.2.6", {"start": v(-12, -30.44) * mm, "end": v(-6.7, -34.28) * mm});
            skLineSegment(sketch, "E17.3.2.6", {"start": v(-17.3, -34.28) * mm, "end": v(-12, -30.44) * mm});
            skPoint(sketch, "E17.6.2.6", {"position": v(-7.72, -37.4) * mm});
            skCircle(sketch, "E17.7.2.6", {"center": v(-12, -36) * mm, "radius": 4.5 * mm, "construction": true});
            skLineSegment(sketch, "E17.9.2.6", {"start": v(-6.7, -34.28) * mm, "end": v(-8.73, -40.5) * mm});
            skLineSegment(sketch, "E17.12.2.6", {"start": v(-8.73, -40.5) * mm, "end": v(-15.27, -40.5) * mm});
            skLineSegment(sketch, "E17.15.2.6", {"start": v(-15.27, -40.5) * mm, "end": v(-17.3, -34.28) * mm});
            skLineSegment(sketch, "E17.0.3.6", {"start": v(0, -30.44) * mm, "end": v(5.3, -34.28) * mm});
            skLineSegment(sketch, "E17.3.3.6", {"start": v(-5.3, -34.28) * mm, "end": v(0, -30.44) * mm});
            skPoint(sketch, "E17.6.3.6", {"position": v(4.28, -37.4) * mm});
            skCircle(sketch, "E17.7.3.6", {"center": v(0, -36) * mm, "radius": 4.5 * mm, "construction": true});
            skLineSegment(sketch, "E17.9.3.6", {"start": v(5.3, -34.28) * mm, "end": v(3.27, -40.5) * mm});
            skLineSegment(sketch, "E17.12.3.6", {"start": v(3.27, -40.5) * mm, "end": v(-3.27, -40.5) * mm});
            skLineSegment(sketch, "E17.15.3.6", {"start": v(-3.27, -40.5) * mm, "end": v(-5.3, -34.28) * mm});
            skLineSegment(sketch, "E17.0.4.6", {"start": v(12, -30.44) * mm, "end": v(17.3, -34.28) * mm});
            skLineSegment(sketch, "E17.3.4.6", {"start": v(6.7, -34.28) * mm, "end": v(12, -30.44) * mm});
            skPoint(sketch, "E17.6.4.6", {"position": v(16.28, -37.4) * mm});
            skCircle(sketch, "E17.7.4.6", {"center": v(12, -36) * mm, "radius": 4.5 * mm, "construction": true});
            skLineSegment(sketch, "E17.9.4.6", {"start": v(17.3, -34.28) * mm, "end": v(15.27, -40.5) * mm});
            skLineSegment(sketch, "E17.12.4.6", {"start": v(15.27, -40.5) * mm, "end": v(8.73, -40.5) * mm});
            skLineSegment(sketch, "E17.15.4.6", {"start": v(8.73, -40.5) * mm, "end": v(6.7, -34.28) * mm});
            skLineSegment(sketch, "E17.0.5.6", {"start": v(24, -30.44) * mm, "end": v(29.3, -34.28) * mm});
            skLineSegment(sketch, "E17.3.5.6", {"start": v(18.7, -34.28) * mm, "end": v(24, -30.44) * mm});
            skPoint(sketch, "E17.6.5.6", {"position": v(28.28, -37.4) * mm});
            skCircle(sketch, "E17.7.5.6", {"center": v(24, -36) * mm, "radius": 4.5 * mm, "construction": true});
            skLineSegment(sketch, "E17.9.5.6", {"start": v(29.3, -34.28) * mm, "end": v(27.27, -40.5) * mm});
            skLineSegment(sketch, "E17.12.5.6", {"start": v(27.27, -40.5) * mm, "end": v(20.73, -40.5) * mm});
            skLineSegment(sketch, "E17.15.5.6", {"start": v(20.73, -40.5) * mm, "end": v(18.7, -34.28) * mm});
            skLineSegment(sketch, "E17.0.6.6", {"start": v(36, -30.44) * mm, "end": v(41.3, -34.28) * mm});
            skLineSegment(sketch, "E17.3.6.6", {"start": v(30.7, -34.28) * mm, "end": v(36, -30.44) * mm});
            skPoint(sketch, "E17.6.6.6", {"position": v(40.28, -37.4) * mm});
            skCircle(sketch, "E17.7.6.6", {"center": v(36, -36) * mm, "radius": 4.5 * mm, "construction": true});
            skLineSegment(sketch, "E17.9.6.6", {"start": v(41.3, -34.28) * mm, "end": v(39.27, -40.5) * mm});
            skLineSegment(sketch, "E17.12.6.6", {"start": v(39.27, -40.5) * mm, "end": v(32.73, -40.5) * mm});
            skLineSegment(sketch, "E17.15.6.6", {"start": v(32.73, -40.5) * mm, "end": v(30.7, -34.28) * mm});
            skSolve(sketch);
        }
        {
            var Q0;
            Q0 = qSketchRegion(id + "F4", true);
            extrude(context, id + "F5", {"entities" : qUnion([Q0]), "operationType" : NewBodyOperationType.REMOVE, "depth" : 1.2 * mm, "offsetDistance" : 25 * mm});
        }
        {
            var Q0;
            Q0=qCreatedBy(makeId("Right.planeOp"),FACE);
            var sketch = newSketch(context, id + "F6", { "sketchPlane" : qUnion([Q0])});
            skCircle(sketch, "E18", {"center": v(-40, 3) * mm, "radius": 1.6 * mm});
            skCircle(sketch, "E19.1.0.0", {"center": v(-20, 3) * mm, "radius": 1.6 * mm});
            skCircle(sketch, "E19.2.0.0", {"center": v(0, 3) * mm, "radius": 1.6 * mm});
            skCircle(sketch, "E19.3.0.0", {"center": v(20, 3) * mm, "radius": 1.6 * mm});
            skCircle(sketch, "E19.4.0.0", {"center": v(40, 3) * mm, "radius": 1.6 * mm});
            skLineSegment(sketch, "E19.direction1", {"start": v(-40, 3) * mm, "end": v(-20, 3) * mm, "construction": true});
            skSolve(sketch);
        }
        {
            var Q0;
            Q0 = qSketchRegion(id + "F6", true);
            extrude(context, id + "F7", {"entities" : qUnion([Q0]), "operationType" : NewBodyOperationType.REMOVE, "endBound" : BoundingType.SYMMETRIC, "oppositeDirection" : true, "depth" : 100 * mm, "offsetDistance" : 25 * mm});
        }
        {
            var Q0;
            Q0=qCreatedBy(makeId("Front.planeOp"),FACE);
            var sketch = newSketch(context, id + "F8", { "sketchPlane" : qUnion([Q0])});
            skCircle(sketch, "E20", {"center": v(-40, 3) * mm, "radius": 1.6 * mm});
            skCircle(sketch, "E21.1.0.0", {"center": v(-20, 3) * mm, "radius": 1.6 * mm});
            skCircle(sketch, "E21.2.0.0", {"center": v(0, 3) * mm, "radius": 1.6 * mm});
            skCircle(sketch, "E21.3.0.0", {"center": v(20, 3) * mm, "radius": 1.6 * mm});
            skCircle(sketch, "E21.4.0.0", {"center": v(40, 3) * mm, "radius": 1.6 * mm});
            skLineSegment(sketch, "E21.direction1", {"start": v(-40, 3) * mm, "end": v(-20, 3) * mm, "construction": true});
            skSolve(sketch);
        }
        {
            var Q0;
            Q0 = qSketchRegion(id + "F8", true);
            extrude(context, id + "F9", {"entities" : qUnion([Q0]), "operationType" : NewBodyOperationType.REMOVE, "endBound" : BoundingType.SYMMETRIC, "oppositeDirection" : true, "depth" : 100 * mm, "offsetDistance" : 25 * mm});
        }
        {
            var Q0;
            Q0=qCreatedBy(makeId("Top.planeOp"),FACE);
            var sketch = newSketch(context, id + "F10", { "sketchPlane" : qUnion([Q0])});
            skCircle(sketch, "E22", {"center": v(-40, 47) * mm, "radius": 1.6 * mm});
            skCircle(sketch, "E23.1.0.0", {"center": v(-20, 47) * mm, "radius": 1.6 * mm});
            skCircle(sketch, "E23.2.0.0", {"center": v(0, 47) * mm, "radius": 1.6 * mm});
            skCircle(sketch, "E23.3.0.0", {"center": v(20, 47) * mm, "radius": 1.6 * mm});
            skCircle(sketch, "E23.4.0.0", {"center": v(40, 47) * mm, "radius": 1.6 * mm});
            skLineSegment(sketch, "E23.direction1", {"start": v(-40, 47) * mm, "end": v(-20, 47) * mm, "construction": true});
            skCircle(sketch, "E24", {"center": v(-47, 40) * mm, "radius": 1.6 * mm});
            skCircle(sketch, "E25.0.1.0", {"center": v(-47, 20) * mm, "radius": 1.6 * mm});
            skCircle(sketch, "E25.0.2.0", {"center": v(-47, 0) * mm, "radius": 1.6 * mm});
            skCircle(sketch, "E25.0.3.0", {"center": v(-47, -20) * mm, "radius": 1.6 * mm});
            skCircle(sketch, "E25.0.4.0", {"center": v(-47, -40) * mm, "radius": 1.6 * mm});
            skLineSegment(sketch, "E25.direction1", {"start": v(-47, 40) * mm, "end": v(-22, 40) * mm, "construction": true});
            skLineSegment(sketch, "E25.direction2", {"start": v(-47, 40) * mm, "end": v(-47, 20) * mm, "construction": true});
            skCircle(sketch, "E26.MirrorC", {"center": v(-40, -47) * mm, "radius": 1.6 * mm});
            skCircle(sketch, "E27.MirrorC", {"center": v(-20, -47) * mm, "radius": 1.6 * mm});
            skCircle(sketch, "E28.MirrorC", {"center": v(20, -47) * mm, "radius": 1.6 * mm});
            skCircle(sketch, "E29.MirrorC", {"center": v(40, -47) * mm, "radius": 1.6 * mm});
            skCircle(sketch, "E30.MirrorC", {"center": v(0, -47) * mm, "radius": 1.6 * mm});
            skLineSegment(sketch, "E31.MirrorCS", {"start": v(-40, -47) * mm, "end": v(-20, -47) * mm, "construction": true});
            skLineSegment(sketch, "E32.MirrorCS", {"start": v(47, 40) * mm, "end": v(47, 20) * mm, "construction": true});
            skCircle(sketch, "E33.MirrorC", {"center": v(47, -20) * mm, "radius": 1.6 * mm});
            skCircle(sketch, "E34.MirrorC", {"center": v(47, 0) * mm, "radius": 1.6 * mm});
            skCircle(sketch, "E35.MirrorC", {"center": v(47, 40) * mm, "radius": 1.6 * mm});
            skCircle(sketch, "E36.MirrorC", {"center": v(47, 20) * mm, "radius": 1.6 * mm});
            skCircle(sketch, "E37.MirrorC", {"center": v(47, -40) * mm, "radius": 1.6 * mm});
            skSolve(sketch);
        }
        {
            var Q0;
            Q0 = qSketchRegion(id + "F10", true);
            extrude(context, id + "F11", {"entities" : qUnion([Q0]), "operationType" : NewBodyOperationType.REMOVE, "depth" : 7 * mm, "offsetDistance" : 25 * mm});
        }
    });
